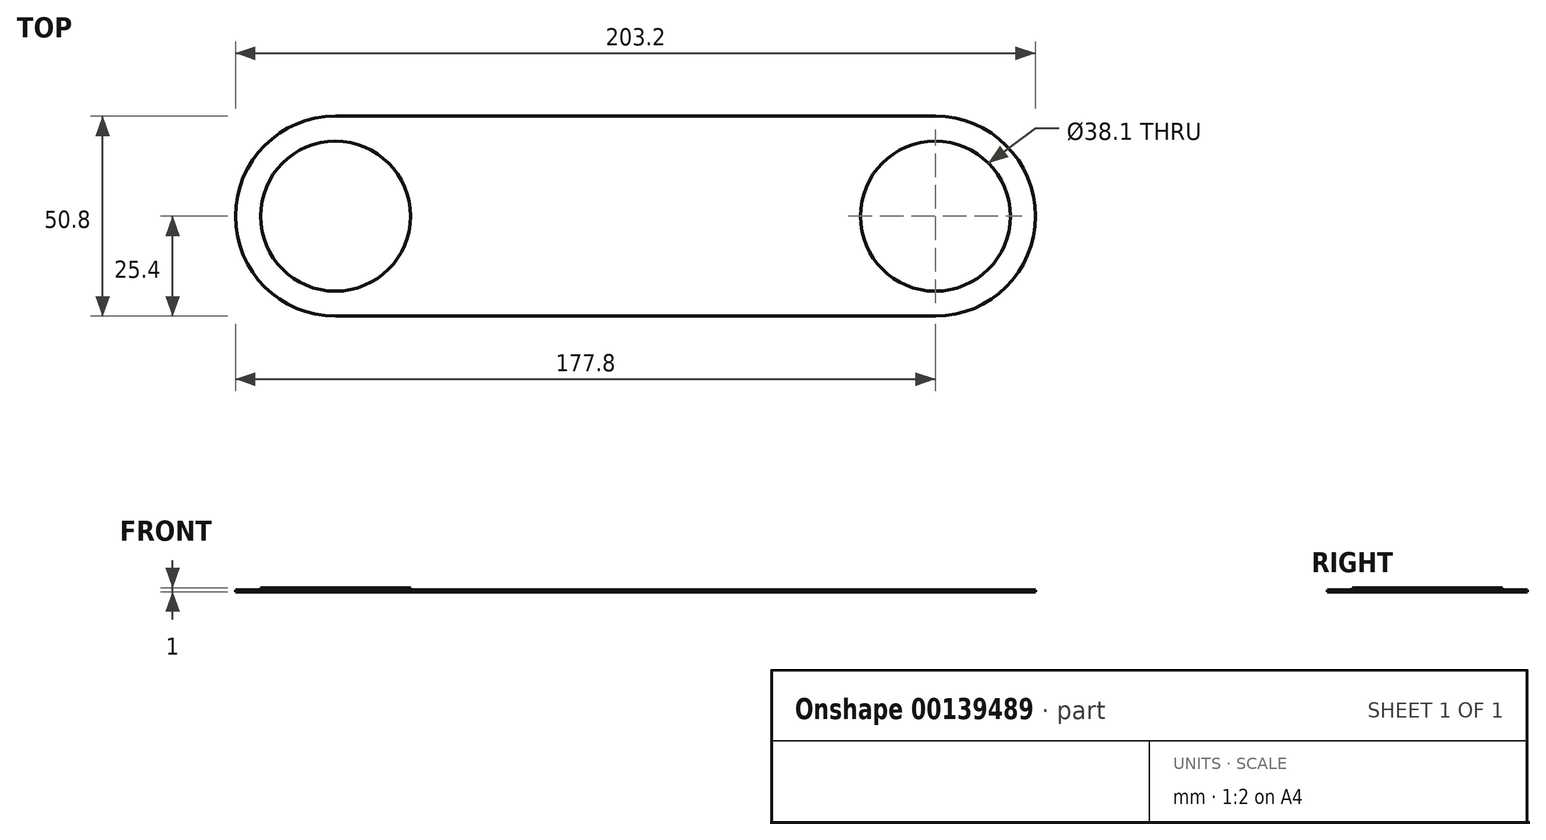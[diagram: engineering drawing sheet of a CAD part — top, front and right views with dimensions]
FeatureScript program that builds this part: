
annotation { "Feature Type Name" : "Feature", "Feature Type Description" : "" }
export const myFeature = defineFeature(function(context is Context, id is Id, definition is map)
    precondition{}
    {
        {
            assignVariable(context, id + "F0", {"name" : "Depth", "anyValue" : .5});
        }
        {
            var Q0;
            Q0=qCreatedBy(makeId("Top.planeOp"),FACE);
            var sketch = newSketch(context, id + "F1", { "sketchPlane" : qUnion([Q0])});
            skLineSegment(sketch, "E0.bottom", {"start": v(76.2, -25.4) * mm, "end": v(-76.2, -25.4) * mm});
            skLineSegment(sketch, "E0.top", {"start": v(76.2, 25.4) * mm, "end": v(-76.2, 25.4) * mm});
            skPoint(sketch, "E0.middle", {"position": v(0, 0) * mm});
            skArc(sketch, "E1", {"start": v(-76.2, 25.4) * mm, "mid": v(-101.6, 0) * mm, "end": v(-76.2, -25.4) * mm});
            skArc(sketch, "E2", {"start": v(76.2, -25.4) * mm, "mid": v(101.6, 0) * mm, "end": v(76.2, 25.4) * mm});
            skSolve(sketch);
        }
        {
            var Q0;
            Q0 = qSketchRegion(id + "F1", true);
            extrude(context, id + "F2", {"entities" : qUnion([Q0]), "depth" : (getVariable(context, 'Depth')) * mm});
        }
        {
            var Q0;
            Q0=makeQuery(id+"F2.opExtrude","CAP_FACE",FACE,{"disambiguationData":[OSD([sQuery(id+"F1.wireOp",EDGE,"E0.bottom"),sQuery(id+"F1.wireOp",EDGE,"E0.top"),sQuery(id+"F1.wireOp",EDGE,"E1"),sQuery(id+"F1.wireOp",EDGE,"E2")])],"isStart":false});
            var sketch = newSketch(context, id + "F3", { "sketchPlane" : qUnion([Q0])});
            skCircle(sketch, "E3", {"center": v(-76.2, 0) * mm, "radius": 19.05 * mm});
            skCircle(sketch, "E4", {"center": v(76.2, 0) * mm, "radius": 19.05 * mm});
            skSolve(sketch);
        }
        {
            var Q0;
            Q0=makeQuery(id+"F3.imprint","IMPRINT",FACE,{"disambiguationData":[TD([[makeQuery(id+"F3.imprint","IMPRINT",EDGE,{"derivedFrom":sQuery(id+"F3.wireOp",EDGE,"E3")}),1.0]])]});
            extrude(context, id + "F4", {"entities" : qUnion([Q0]), "operationType" : NewBodyOperationType.ADD, "depth" : (getVariable(context, 'Depth')) * mm});
        }
        {
            var Q0;
            Q0=makeQuery(id+"F3.imprint","IMPRINT",FACE,{"disambiguationData":[TD([[makeQuery(id+"F3.imprint","IMPRINT",EDGE,{"derivedFrom":sQuery(id+"F3.wireOp",EDGE,"E4")}),1.0]])]});
            var Q1;
            Q1=sQuery(id+"F3.wireOp",EDGE,"E4");
            extrude(context, id + "F5", {"entities" : qUnion([Q0]), "operationType" : NewBodyOperationType.REMOVE, "surfaceEntities" : qUnion([Q1]), "oppositeDirection" : true, "depth" : (getVariable(context, 'Depth')) * mm});
        }
    });
